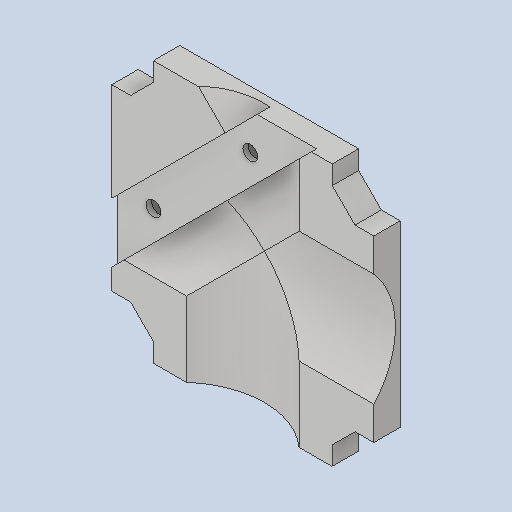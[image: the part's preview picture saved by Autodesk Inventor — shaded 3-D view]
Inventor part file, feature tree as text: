
AUTODESK INVENTOR PART (.ipt)
format: ipt  version: 2023 (Build 270158000, 158)  size: 362,496 bytes
history: native  units: mm
features: reference x16, sketch x12, extrude x11, other x9, projected_geometry x6, plane x5, hole x2
ambient origin geometry x8: Origin, YZ Plane, XZ Plane, XY Plane, X Axis, Y Axis, Z Axis, Center Point
bodies: Solid1 (feature_tree)
feature tree (61):
  plane  "Work Plane1"
  extrude  "Extrusion1"  Depth=5.0mm
  extrude  "Extrusion4"  Depth=53.8mm
  hole  "Hole1"  [1 undecoded]
  extrude  "Extrusion5"  Depth=20.0mm
  plane  "Work Plane3"
  sketch  "Sketch7"  dims[d30=20.0mm d31=20.0mm]
  plane  "Work Plane4"
  extrude  "Extrusion6"  Depth=2.8mm
  extrude  "Extrusion7"  Depth=2.8mm
  hole  "Hole2"  [1 undecoded]
  extrude  "Extrusion10"  Depth=0.1mm
  extrude  "Extrusion11"  Depth=8.0mm
  sketch  "Skizze15"  dims[d45=20.0mm]
  plane  "Arbeitsebene5"
  extrude  "Extrusion12"  Depth=30.0mm
  sketch  "Skizze16"  dims[d46=2.8mm d47=6.0mm d48=6.0mm d49=2.5mm d50=90.0deg d51=12.0mm d52=0.0mm d53=2.0mm d54=28.0mm d55=0.0mm d56=2.0mm d57=28.0mm d58=0.0mm d59=15.0mm d60=10.0mm d61=0.0mm d62=2.8mm d64=2.8mm d65=6.0mm d66=5.5mm d67=3.0mm d68=90.0deg d69=12.0mm d70=0.0mm d71=29.0mm d72=0.0mm d73=4.0mm d74=29.0mm d75=0.0mm d76=29.0mm d77=0.0mm d78=0.2mm d79=10.0mm d80=0.0mm d81=32.0mm d82=32.0mm d83=0.0mm d84=0.0mm d85=32.0mm d86=10.0mm d87=0.0mm]
  plane  "Arbeitsebene6"
  extrude  "Extrusion13"  Depth=2.0mm
  extrude  "Extrusion8"  Depth=10.0mm TaperAngle=0.0deg
  extrude  "Extrusion9"  Depth=2.0mm
  sketch  "Sketch1"  dims[d10=5.0mm d11=0.0mm d18=53.8mm]
  reference  "Reference1"
  reference  "Reference2"
  reference  "Reference3"
  reference  "Reference4"
  reference  "Reference9"
  reference  "Reference20"
  reference  "Reference21"
  reference  "Reference22"
  reference  "Reference23"
  reference  "Reference24"
  sketch  "Sketch4"  dims[d19=45.0deg d20=53.8mm]
  projected_geometry  "Projected Loop1"
  reference  "Reference25"
  reference  "Reference26"
  projected_geometry  "Projected Loop2"
  sketch  "Sketch6"  dims[d21=45.0mm d22=45.0mm]
  reference  "Reference27"
  reference  "Reference28"
  reference  "Reference29"
  reference  "Reference30"
  sketch  "Sketch8"  dims[d32=2.8mm d33=2.8mm]
  sketch  "Sketch9"  dims[d34=2.8mm d35=2.8mm]
  sketch  "Sketch11"  dims[d36=0.1mm d37=0.1mm]
  projected_geometry  "Projected Loop3"
  sketch  "Sketch12"  dims[d38=0.1mm d39=0.1mm]
  sketch  "Sketch13"  dims[d40=45.0deg d41=8.0mm]
  projected_geometry  "Projected Loop5"
  sketch  "Sketch14"  dims[d42=28.0mm d43=0.0mm d44=30.0mm]
  projected_geometry  "Projected Loop6"
  projected_geometry  "Projizierte Kontur7"
  other  "Assembly_Cube_v2_Thorlabs.iam"
  other  "10_Cube_Base:1"
  other  "00_Base_v0:1"
  other  "Assembly_Cube_Kinematic_Mirrormount_45_v2.iam"
  other  "Assembly_Cube_empty_1x1_v2:1"
  other  "10_Cube_1x1_v2:1"
  other  "10_Lid_1x1_v2:1"
  other  "DIN 912 - ersetzt durch DIN EN ISO 4762 M3 x 12:7"
  other  "10_Cube_Lid:1"
note: 2 required parameter values undecoded (feature->parameter linkage not recoverable at this tier; creation-order binding heuristic only, values carry confidence <= 0.55)
